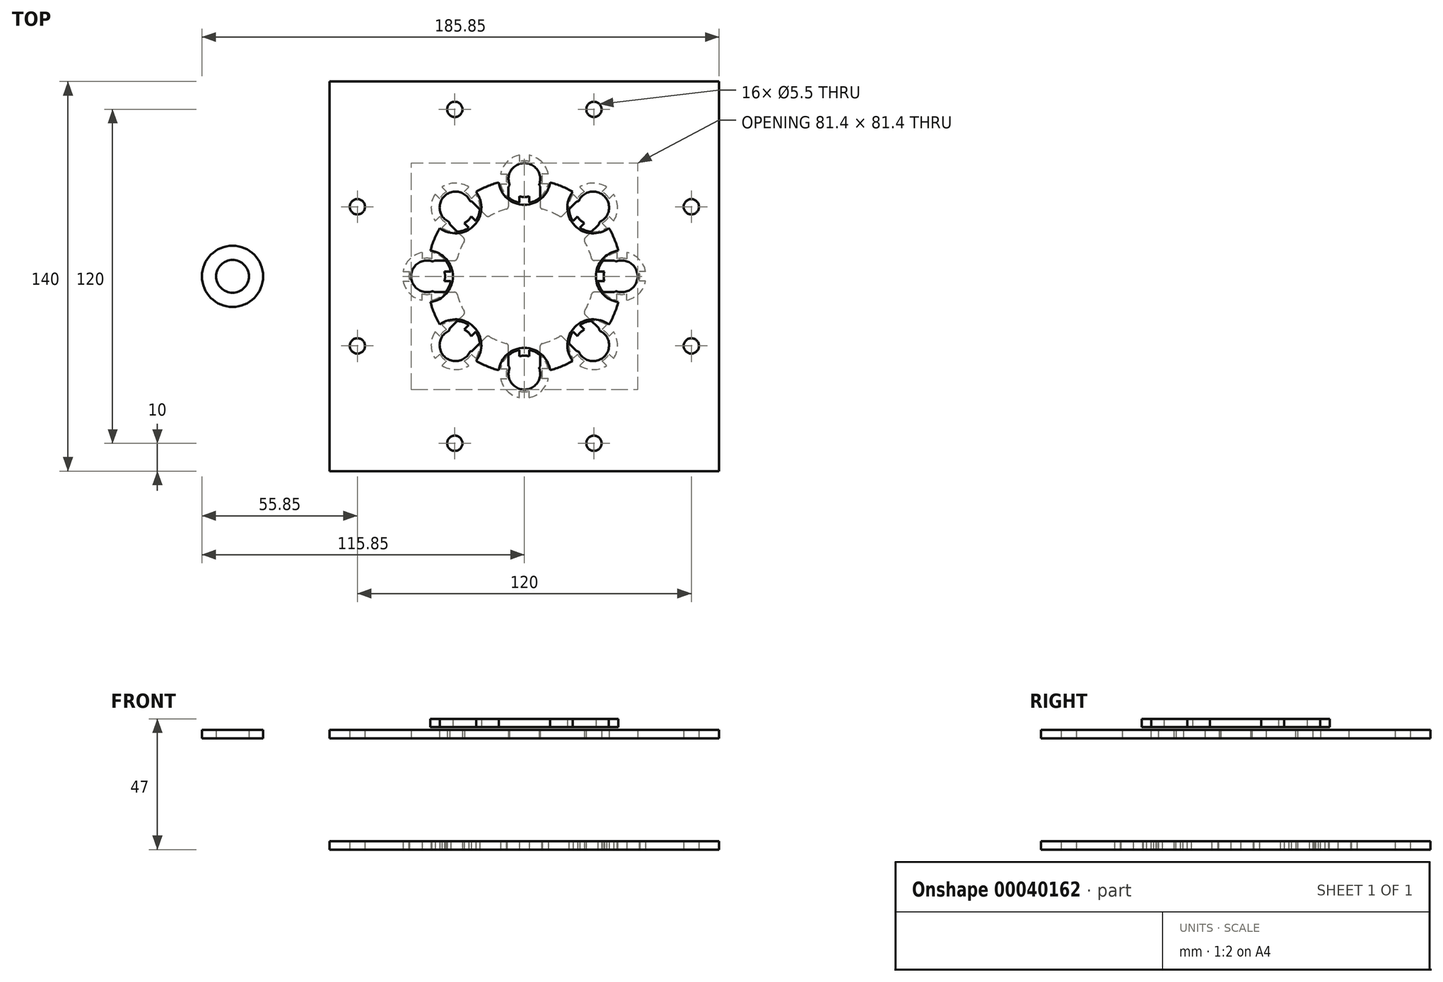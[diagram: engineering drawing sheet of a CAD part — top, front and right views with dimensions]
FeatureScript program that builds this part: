
annotation { "Feature Type Name" : "Feature", "Feature Type Description" : "" }
export const myFeature = defineFeature(function(context is Context, id is Id, definition is map)
    precondition{}
    {
        {
            var Q0;
            Q0=qCreatedBy(makeId("Top.planeOp"),FACE);
            var sketch = newSketch(context, id + "F0", { "sketchPlane" : qUnion([Q0])});
            skCircle(sketch, "E0", {"center": v(0, 0) * mm, "radius": 35 * mm, "construction": true});
            skCircle(sketch, "E1", {"center": v(0, 35) * mm, "radius": 5.7 * mm, "construction": true});
            skLineSegment(sketch, "E2.rect.bottom", {"start": v(70, 70) * mm, "end": v(-70, 70) * mm});
            skLineSegment(sketch, "E2.rect.top", {"start": v(70, -70) * mm, "end": v(-70, -70) * mm});
            skLineSegment(sketch, "E2.rect.left", {"start": v(70, 70) * mm, "end": v(70, -70) * mm});
            skLineSegment(sketch, "E2.rect.right", {"start": v(-70, 70) * mm, "end": v(-70, -70) * mm});
            skLineSegment(sketch, "E3", {"start": v(-50, 70) * mm, "end": v(-50, -70) * mm, "construction": true});
            skLineSegment(sketch, "E4", {"start": v(-70, 50) * mm, "end": v(70, 50) * mm, "construction": true});
            skLineSegment(sketch, "E5", {"start": v(-5.7, 35) * mm, "end": v(-5.7, 24.34) * mm, "construction": true});
            skLineSegment(sketch, "E6", {"start": v(5.7, 35) * mm, "end": v(5.7, 24.34) * mm, "construction": true});
            skPoint(sketch, "E7", {"position": v(-5.7, 24.34) * mm});
            skCircle(sketch, "E8", {"center": v(0, 0) * mm, "radius": 25 * mm, "construction": true});
            skLineSegment(sketch, "E9", {"start": v(-5.7, 32.2) * mm, "end": v(-5.3, 32.9) * mm});
            skLineSegment(sketch, "E10.MirrorCS", {"start": v(5.7, 32.2) * mm, "end": v(5.3, 32.9) * mm});
            skArc(sketch, "E11", {"start": v(5.3, 32.9) * mm, "mid": v(0, 40.7) * mm, "end": v(-5.3, 32.9) * mm});
            skLineSegment(sketch, "E12", {"start": v(-5.7, 32.2) * mm, "end": v(-5.7, 24.34) * mm});
            skLineSegment(sketch, "E13", {"start": v(5.7, 32.2) * mm, "end": v(5.7, 24.34) * mm});
            skLineSegment(sketch, "E14.1.0", {"start": v(-18.75, 26.8) * mm, "end": v(-13.18, 21.24) * mm});
            skLineSegment(sketch, "E14.1.1", {"start": v(-26.8, 18.75) * mm, "end": v(-21.24, 13.18) * mm});
            skLineSegment(sketch, "E14.1.2", {"start": v(-26.8, 18.75) * mm, "end": v(-27.01, 19.52) * mm});
            skLineSegment(sketch, "E14.1.3", {"start": v(-18.75, 26.8) * mm, "end": v(-19.52, 27.01) * mm});
            skArc(sketch, "E14.1.4", {"start": v(-19.52, 27.01) * mm, "mid": v(-28.78, 28.78) * mm, "end": v(-27.01, 19.52) * mm});
            skLineSegment(sketch, "E14.2.0", {"start": v(-32.2, 5.7) * mm, "end": v(-24.34, 5.7) * mm});
            skLineSegment(sketch, "E14.2.1", {"start": v(-32.2, -5.7) * mm, "end": v(-24.34, -5.7) * mm});
            skLineSegment(sketch, "E14.2.2", {"start": v(-32.2, -5.7) * mm, "end": v(-32.9, -5.3) * mm});
            skLineSegment(sketch, "E14.2.3", {"start": v(-32.2, 5.7) * mm, "end": v(-32.9, 5.3) * mm});
            skArc(sketch, "E14.2.4", {"start": v(-32.9, 5.3) * mm, "mid": v(-40.7, 0) * mm, "end": v(-32.9, -5.3) * mm});
            skLineSegment(sketch, "E14.3.0", {"start": v(-26.8, -18.75) * mm, "end": v(-21.24, -13.18) * mm});
            skLineSegment(sketch, "E14.3.1", {"start": v(-18.75, -26.8) * mm, "end": v(-13.18, -21.24) * mm});
            skLineSegment(sketch, "E14.3.2", {"start": v(-18.75, -26.8) * mm, "end": v(-19.52, -27.01) * mm});
            skLineSegment(sketch, "E14.3.3", {"start": v(-26.8, -18.75) * mm, "end": v(-27.01, -19.52) * mm});
            skArc(sketch, "E14.3.4", {"start": v(-27.01, -19.52) * mm, "mid": v(-28.78, -28.78) * mm, "end": v(-19.52, -27.01) * mm});
            skLineSegment(sketch, "E14.4.0", {"start": v(-5.7, -32.2) * mm, "end": v(-5.7, -24.34) * mm});
            skLineSegment(sketch, "E14.4.1", {"start": v(5.7, -32.2) * mm, "end": v(5.7, -24.34) * mm});
            skLineSegment(sketch, "E14.4.2", {"start": v(5.7, -32.2) * mm, "end": v(5.3, -32.9) * mm});
            skLineSegment(sketch, "E14.4.3", {"start": v(-5.7, -32.2) * mm, "end": v(-5.3, -32.9) * mm});
            skArc(sketch, "E14.4.4", {"start": v(-5.3, -32.9) * mm, "mid": v(0, -40.7) * mm, "end": v(5.3, -32.9) * mm});
            skLineSegment(sketch, "E14.5.0", {"start": v(18.75, -26.8) * mm, "end": v(13.18, -21.24) * mm});
            skLineSegment(sketch, "E14.5.1", {"start": v(26.8, -18.75) * mm, "end": v(21.24, -13.18) * mm});
            skLineSegment(sketch, "E14.5.2", {"start": v(26.8, -18.75) * mm, "end": v(27.01, -19.52) * mm});
            skLineSegment(sketch, "E14.5.3", {"start": v(18.75, -26.8) * mm, "end": v(19.52, -27.01) * mm});
            skArc(sketch, "E14.5.4", {"start": v(19.52, -27.01) * mm, "mid": v(28.78, -28.78) * mm, "end": v(27.01, -19.52) * mm});
            skLineSegment(sketch, "E14.6.0", {"start": v(32.2, -5.7) * mm, "end": v(24.34, -5.7) * mm});
            skLineSegment(sketch, "E14.6.1", {"start": v(32.2, 5.7) * mm, "end": v(24.34, 5.7) * mm});
            skLineSegment(sketch, "E14.6.2", {"start": v(32.2, 5.7) * mm, "end": v(32.9, 5.3) * mm});
            skLineSegment(sketch, "E14.6.3", {"start": v(32.2, -5.7) * mm, "end": v(32.9, -5.3) * mm});
            skArc(sketch, "E14.6.4", {"start": v(32.9, -5.3) * mm, "mid": v(40.7, 0) * mm, "end": v(32.9, 5.3) * mm});
            skLineSegment(sketch, "E14.7.0", {"start": v(26.8, 18.75) * mm, "end": v(21.24, 13.18) * mm});
            skLineSegment(sketch, "E14.7.1", {"start": v(18.75, 26.8) * mm, "end": v(13.18, 21.24) * mm});
            skLineSegment(sketch, "E14.7.2", {"start": v(18.75, 26.8) * mm, "end": v(19.52, 27.01) * mm});
            skLineSegment(sketch, "E14.7.3", {"start": v(26.8, 18.75) * mm, "end": v(27.01, 19.52) * mm});
            skArc(sketch, "E14.7.4", {"start": v(27.01, 19.52) * mm, "mid": v(28.78, 28.78) * mm, "end": v(19.52, 27.01) * mm});
            skArc(sketch, "E15", {"start": v(-5.7, 24.34) * mm, "mid": v(-9.57, 23.1) * mm, "end": v(-13.18, 21.24) * mm});
            skArc(sketch, "E16", {"start": v(13.18, 21.24) * mm, "mid": v(9.57, 23.1) * mm, "end": v(5.7, 24.34) * mm});
            skArc(sketch, "E17", {"start": v(24.34, 5.7) * mm, "mid": v(23.1, 9.57) * mm, "end": v(21.24, 13.18) * mm});
            skArc(sketch, "E18", {"start": v(-21.24, 13.18) * mm, "mid": v(-23.1, 9.57) * mm, "end": v(-24.34, 5.7) * mm});
            skArc(sketch, "E19", {"start": v(-24.34, -5.7) * mm, "mid": v(-23.1, -9.57) * mm, "end": v(-21.24, -13.18) * mm});
            skArc(sketch, "E20", {"start": v(-13.18, -21.24) * mm, "mid": v(-9.57, -23.1) * mm, "end": v(-5.7, -24.34) * mm});
            skArc(sketch, "E21", {"start": v(5.7, -24.34) * mm, "mid": v(9.57, -23.1) * mm, "end": v(13.18, -21.24) * mm});
            skArc(sketch, "E22", {"start": v(21.24, -13.18) * mm, "mid": v(23.1, -9.57) * mm, "end": v(24.34, -5.7) * mm});
            skLineSegment(sketch, "E23.rect.bottom", {"start": v(60, 60) * mm, "end": v(-60, 60) * mm, "construction": true});
            skLineSegment(sketch, "E23.rect.top", {"start": v(60, -60) * mm, "end": v(-60, -60) * mm, "construction": true});
            skLineSegment(sketch, "E23.rect.left", {"start": v(60, 60) * mm, "end": v(60, -60) * mm, "construction": true});
            skLineSegment(sketch, "E23.rect.right", {"start": v(-60, 60) * mm, "end": v(-60, -60) * mm, "construction": true});
            skCircle(sketch, "E24", {"center": v(-25, 60) * mm, "radius": 2.75 * mm});
            skCircle(sketch, "E25.MirrorC", {"center": v(25, 60) * mm, "radius": 2.75 * mm});
            skCircle(sketch, "E26.MirrorC", {"center": v(25, -60) * mm, "radius": 2.75 * mm});
            skCircle(sketch, "E27.MirrorC", {"center": v(-25, -60) * mm, "radius": 2.75 * mm});
            skCircle(sketch, "E28", {"center": v(-60, 25) * mm, "radius": 2.75 * mm});
            skCircle(sketch, "E29.MirrorC", {"center": v(-60, -25) * mm, "radius": 2.75 * mm});
            skCircle(sketch, "E30.MirrorC", {"center": v(60, 25) * mm, "radius": 2.75 * mm});
            skCircle(sketch, "E31.MirrorC", {"center": v(60, -25) * mm, "radius": 2.75 * mm});
            skSolve(sketch);
        }
        {
            var Q0;
            Q0=makeQuery(id+"F0.imprint","IMPRINT",FACE,{"disambiguationData":[TD([[makeQuery(id+"F0.imprint","IMPRINT",EDGE,{"derivedFrom":sQuery(id+"F0.wireOp",EDGE,"E2.rect.bottom")}),1.0]])]});
            extrude(context, id + "F1", {"entities" : qUnion([Q0]), "depth" : 3 * mm});
        }
        {
            var Q0;
            Q0=makeQuery(id+"F1.opExtrude","SWEPT_EDGE",EDGE,{"disambiguationData":[OSD([sQuery(id+"F0.wireOp",EDGE,"E14.1.1"),sQuery(id+"F0.wireOp",EDGE,"E18")])]});
            var Q1;
            Q1=makeQuery(id+"F1.opExtrude","SWEPT_EDGE",EDGE,{"disambiguationData":[OSD([sQuery(id+"F0.wireOp",EDGE,"E14.2.1"),sQuery(id+"F0.wireOp",EDGE,"E19")])]});
            var Q2;
            Q2=makeQuery(id+"F1.opExtrude","SWEPT_EDGE",EDGE,{"disambiguationData":[OSD([sQuery(id+"F0.wireOp",EDGE,"E14.3.0"),sQuery(id+"F0.wireOp",EDGE,"E19")])]});
            var Q3;
            Q3=makeQuery(id+"F1.opExtrude","SWEPT_EDGE",EDGE,{"disambiguationData":[OSD([sQuery(id+"F0.wireOp",EDGE,"E14.2.0"),sQuery(id+"F0.wireOp",EDGE,"E18")])]});
            var Q4;
            Q4=makeQuery(id+"F1.opExtrude","SWEPT_EDGE",EDGE,{"disambiguationData":[OSD([sQuery(id+"F0.wireOp",EDGE,"E14.1.0"),sQuery(id+"F0.wireOp",EDGE,"E15")])]});
            var Q5;
            Q5=makeQuery(id+"F1.opExtrude","SWEPT_EDGE",EDGE,{"disambiguationData":[OSD([sQuery(id+"F0.wireOp",EDGE,"E12"),sQuery(id+"F0.wireOp",EDGE,"E15")])]});
            var Q6;
            Q6=makeQuery(id+"F1.opExtrude","SWEPT_EDGE",EDGE,{"disambiguationData":[OSD([sQuery(id+"F0.wireOp",EDGE,"E14.4.0"),sQuery(id+"F0.wireOp",EDGE,"E20")])]});
            var Q7;
            Q7=makeQuery(id+"F1.opExtrude","SWEPT_EDGE",EDGE,{"disambiguationData":[OSD([sQuery(id+"F0.wireOp",EDGE,"E14.3.1"),sQuery(id+"F0.wireOp",EDGE,"E20")])]});
            var Q8;
            Q8=makeQuery(id+"F1.opExtrude","SWEPT_EDGE",EDGE,{"disambiguationData":[OSD([sQuery(id+"F0.wireOp",EDGE,"E14.5.0"),sQuery(id+"F0.wireOp",EDGE,"E21")])]});
            var Q9;
            Q9=makeQuery(id+"F1.opExtrude","SWEPT_EDGE",EDGE,{"disambiguationData":[OSD([sQuery(id+"F0.wireOp",EDGE,"E14.4.1"),sQuery(id+"F0.wireOp",EDGE,"E21")])]});
            var Q10;
            Q10=makeQuery(id+"F1.opExtrude","SWEPT_EDGE",EDGE,{"disambiguationData":[OSD([sQuery(id+"F0.wireOp",EDGE,"E14.5.1"),sQuery(id+"F0.wireOp",EDGE,"E22")])]});
            var Q11;
            Q11=makeQuery(id+"F1.opExtrude","SWEPT_EDGE",EDGE,{"disambiguationData":[OSD([sQuery(id+"F0.wireOp",EDGE,"E14.6.0"),sQuery(id+"F0.wireOp",EDGE,"E22")])]});
            var Q12;
            Q12=makeQuery(id+"F1.opExtrude","SWEPT_EDGE",EDGE,{"disambiguationData":[OSD([sQuery(id+"F0.wireOp",EDGE,"E14.6.1"),sQuery(id+"F0.wireOp",EDGE,"E17")])]});
            var Q13;
            Q13=makeQuery(id+"F1.opExtrude","SWEPT_EDGE",EDGE,{"disambiguationData":[OSD([sQuery(id+"F0.wireOp",EDGE,"E14.7.0"),sQuery(id+"F0.wireOp",EDGE,"E17")])]});
            var Q14;
            Q14=makeQuery(id+"F1.opExtrude","SWEPT_EDGE",EDGE,{"disambiguationData":[OSD([sQuery(id+"F0.wireOp",EDGE,"E14.7.1"),sQuery(id+"F0.wireOp",EDGE,"E16")])]});
            var Q15;
            Q15=makeQuery(id+"F1.opExtrude","SWEPT_EDGE",EDGE,{"disambiguationData":[OSD([sQuery(id+"F0.wireOp",EDGE,"E13"),sQuery(id+"F0.wireOp",EDGE,"E16")])]});
            fillet(context, id + "F2", {"entities" : qUnion([Q0, Q1, Q2, Q3, Q4, Q5, Q6, Q7, Q8, Q9, Q10, Q11, Q12, Q13, Q14, Q15]), "radius" : 1 * mm, "tangentPropagation" : true, "allowEdgeOverflow" : false});
        }
        {
            var Q0;
            Q0=qCreatedBy(makeId("Top.planeOp"),FACE);
            cPlane(context, id + "F3", {"entities" : qUnion([Q0]), "cplaneType" : CPlaneType.OFFSET, "offset" : 40 * mm, "oppositeDirection" : true, "width" : 150 * mm, "height" : 150 * mm});
        }
        {
            var Q0;
            Q0=qCreatedBy(id+"F3.planeOp",FACE);
            var sketch = newSketch(context, id + "F4", { "sketchPlane" : qUnion([Q0])});
            skArc(sketch, "E32", {"start": v(8.57, -33.25) * mm, "mid": v(6.19, -28.81) * mm, "end": v(1.75, -26.43) * mm});
            skLineSegment(sketch, "E33.rect.right", {"start": v(1.75, -26.43) * mm, "end": v(1.75, -28.74) * mm});
            skArc(sketch, "E34", {"start": v(1.75, -28.74) * mm, "mid": v(0, -28.5) * mm, "end": v(-1.75, -28.74) * mm});
            skLineSegment(sketch, "E33.rect.left", {"start": v(-1.75, -26.43) * mm, "end": v(-1.75, -28.74) * mm});
            skArc(sketch, "E35", {"start": v(-1.75, -26.43) * mm, "mid": v(-6.19, -28.81) * mm, "end": v(-8.57, -33.25) * mm});
            skLineSegment(sketch, "E36.1.1", {"start": v(-8.57, -33.25) * mm, "end": v(-6.26, -33.25) * mm});
            skArc(sketch, "E36.1.2", {"start": v(-6.26, -33.25) * mm, "mid": v(-6.5, -35) * mm, "end": v(-6.26, -36.75) * mm});
            skArc(sketch, "E37", {"start": v(-1.75, -28.74) * mm, "mid": v(0, -41.5) * mm, "end": v(1.75, -28.74) * mm, "construction": true});
            skLineSegment(sketch, "E36.1.0", {"start": v(-8.57, -36.75) * mm, "end": v(-6.26, -36.75) * mm});
            skArc(sketch, "E38", {"start": v(-8.57, -33.25) * mm, "mid": v(-8.75, -35) * mm, "end": v(-8.57, -36.75) * mm, "construction": true});
            skArc(sketch, "E39", {"start": v(-8.57, -36.75) * mm, "mid": v(-6.19, -41.19) * mm, "end": v(-1.75, -43.57) * mm});
            skLineSegment(sketch, "E36.2.1", {"start": v(-1.75, -43.57) * mm, "end": v(-1.75, -41.26) * mm});
            skArc(sketch, "E36.2.2", {"start": v(-1.75, -41.26) * mm, "mid": v(0, -41.5) * mm, "end": v(1.75, -41.26) * mm});
            skLineSegment(sketch, "E36.2.0", {"start": v(1.75, -43.57) * mm, "end": v(1.75, -41.26) * mm});
            skArc(sketch, "E40", {"start": v(-1.75, -43.57) * mm, "mid": v(0, -43.75) * mm, "end": v(1.75, -43.57) * mm, "construction": true});
            skArc(sketch, "E41", {"start": v(1.75, -43.57) * mm, "mid": v(6.19, -41.19) * mm, "end": v(8.57, -36.75) * mm});
            skLineSegment(sketch, "E36.3.1", {"start": v(8.57, -36.75) * mm, "end": v(6.26, -36.75) * mm});
            skArc(sketch, "E42", {"start": v(8.57, -36.75) * mm, "mid": v(8.75, -35) * mm, "end": v(8.57, -33.25) * mm, "construction": true});
            skLineSegment(sketch, "E36.3.0", {"start": v(8.57, -33.25) * mm, "end": v(6.26, -33.25) * mm});
            skArc(sketch, "E36.3.2", {"start": v(6.26, -36.75) * mm, "mid": v(6.5, -35) * mm, "end": v(6.26, -33.25) * mm});
            skLineSegment(sketch, "E33.rect.bottom", {"start": v(-1.75, -26.43) * mm, "end": v(1.75, -26.43) * mm, "construction": true});
            skArc(sketch, "E43", {"start": v(1.75, -26.43) * mm, "mid": v(0, -26.25) * mm, "end": v(-1.75, -26.43) * mm, "construction": true});
            skLineSegment(sketch, "E33.rect.top", {"start": v(-1.75, -28.74) * mm, "end": v(1.75, -28.74) * mm, "construction": true});
            skLineSegment(sketch, "E44.rect.bottom", {"start": v(70, -70) * mm, "end": v(-70, -70) * mm});
            skLineSegment(sketch, "E44.rect.top", {"start": v(70, 70) * mm, "end": v(-70, 70) * mm});
            skLineSegment(sketch, "E44.rect.left", {"start": v(70, -70) * mm, "end": v(70, 70) * mm});
            skLineSegment(sketch, "E44.rect.right", {"start": v(-70, -70) * mm, "end": v(-70, 70) * mm});
            skPoint(sketch, "E44.rect.middle", {"position": v(0, 0) * mm});
            skLineSegment(sketch, "E45.1.1", {"start": v(29.57, -17.45) * mm, "end": v(27.94, -19.08) * mm});
            skArc(sketch, "E45.1.2", {"start": v(30.41, -21.56) * mm, "mid": v(29.34, -20.15) * mm, "end": v(27.94, -19.08) * mm});
            skLineSegment(sketch, "E45.1.3", {"start": v(32.05, -19.92) * mm, "end": v(30.41, -21.56) * mm});
            skArc(sketch, "E45.1.4", {"start": v(32.05, -29.57) * mm, "mid": v(33.5, -24.75) * mm, "end": v(32.05, -19.92) * mm});
            skArc(sketch, "E45.1.5", {"start": v(29.57, -17.45) * mm, "mid": v(24.75, -16) * mm, "end": v(19.92, -17.45) * mm});
            skLineSegment(sketch, "E45.1.6", {"start": v(19.92, -17.45) * mm, "end": v(21.56, -19.08) * mm});
            skArc(sketch, "E45.1.7", {"start": v(21.56, -19.08) * mm, "mid": v(20.15, -20.15) * mm, "end": v(19.08, -21.56) * mm});
            skLineSegment(sketch, "E45.1.8", {"start": v(17.45, -19.92) * mm, "end": v(19.08, -21.56) * mm});
            skArc(sketch, "E45.1.9", {"start": v(17.45, -19.92) * mm, "mid": v(16, -24.75) * mm, "end": v(17.45, -29.57) * mm});
            skLineSegment(sketch, "E45.1.10", {"start": v(17.45, -29.57) * mm, "end": v(19.08, -27.94) * mm});
            skArc(sketch, "E45.1.11", {"start": v(19.08, -27.94) * mm, "mid": v(20.15, -29.34) * mm, "end": v(21.56, -30.41) * mm});
            skLineSegment(sketch, "E45.1.12", {"start": v(19.92, -32.05) * mm, "end": v(21.56, -30.41) * mm});
            skArc(sketch, "E45.1.13", {"start": v(19.92, -32.05) * mm, "mid": v(24.75, -33.5) * mm, "end": v(29.57, -32.05) * mm});
            skArc(sketch, "E45.1.14", {"start": v(27.94, -30.41) * mm, "mid": v(29.34, -29.34) * mm, "end": v(30.41, -27.94) * mm});
            skLineSegment(sketch, "E45.1.15", {"start": v(29.57, -32.05) * mm, "end": v(27.94, -30.41) * mm});
            skLineSegment(sketch, "E45.1.16", {"start": v(32.05, -29.57) * mm, "end": v(30.41, -27.94) * mm});
            skLineSegment(sketch, "E45.2.1", {"start": v(33.25, 8.57) * mm, "end": v(33.25, 6.26) * mm});
            skArc(sketch, "E45.2.2", {"start": v(36.75, 6.26) * mm, "mid": v(35, 6.5) * mm, "end": v(33.25, 6.26) * mm});
            skLineSegment(sketch, "E45.2.3", {"start": v(36.75, 8.57) * mm, "end": v(36.75, 6.26) * mm});
            skArc(sketch, "E45.2.4", {"start": v(43.57, 1.75) * mm, "mid": v(41.19, 6.19) * mm, "end": v(36.75, 8.57) * mm});
            skArc(sketch, "E45.2.5", {"start": v(33.25, 8.57) * mm, "mid": v(28.81, 6.19) * mm, "end": v(26.43, 1.75) * mm});
            skLineSegment(sketch, "E45.2.6", {"start": v(26.43, 1.75) * mm, "end": v(28.74, 1.75) * mm});
            skArc(sketch, "E45.2.7", {"start": v(28.74, 1.75) * mm, "mid": v(28.5, 0) * mm, "end": v(28.74, -1.75) * mm});
            skLineSegment(sketch, "E45.2.8", {"start": v(26.43, -1.75) * mm, "end": v(28.74, -1.75) * mm});
            skArc(sketch, "E45.2.9", {"start": v(26.43, -1.75) * mm, "mid": v(28.81, -6.19) * mm, "end": v(33.25, -8.57) * mm});
            skLineSegment(sketch, "E45.2.10", {"start": v(33.25, -8.57) * mm, "end": v(33.25, -6.26) * mm});
            skArc(sketch, "E45.2.11", {"start": v(33.25, -6.26) * mm, "mid": v(35, -6.5) * mm, "end": v(36.75, -6.26) * mm});
            skLineSegment(sketch, "E45.2.12", {"start": v(36.75, -8.57) * mm, "end": v(36.75, -6.26) * mm});
            skArc(sketch, "E45.2.13", {"start": v(36.75, -8.57) * mm, "mid": v(41.19, -6.19) * mm, "end": v(43.57, -1.75) * mm});
            skArc(sketch, "E45.2.14", {"start": v(41.26, -1.75) * mm, "mid": v(41.5, 0) * mm, "end": v(41.26, 1.75) * mm});
            skLineSegment(sketch, "E45.2.15", {"start": v(43.57, -1.75) * mm, "end": v(41.26, -1.75) * mm});
            skLineSegment(sketch, "E45.2.16", {"start": v(43.57, 1.75) * mm, "end": v(41.26, 1.75) * mm});
            skLineSegment(sketch, "E45.3.1", {"start": v(17.45, 29.57) * mm, "end": v(19.08, 27.94) * mm});
            skArc(sketch, "E45.3.2", {"start": v(21.56, 30.41) * mm, "mid": v(20.15, 29.34) * mm, "end": v(19.08, 27.94) * mm});
            skLineSegment(sketch, "E45.3.3", {"start": v(19.92, 32.05) * mm, "end": v(21.56, 30.41) * mm});
            skArc(sketch, "E45.3.4", {"start": v(29.57, 32.05) * mm, "mid": v(24.75, 33.5) * mm, "end": v(19.92, 32.05) * mm});
            skArc(sketch, "E45.3.5", {"start": v(17.45, 29.57) * mm, "mid": v(16, 24.75) * mm, "end": v(17.45, 19.92) * mm});
            skLineSegment(sketch, "E45.3.6", {"start": v(17.45, 19.92) * mm, "end": v(19.08, 21.56) * mm});
            skArc(sketch, "E45.3.7", {"start": v(19.08, 21.56) * mm, "mid": v(20.15, 20.15) * mm, "end": v(21.56, 19.08) * mm});
            skLineSegment(sketch, "E45.3.8", {"start": v(19.92, 17.45) * mm, "end": v(21.56, 19.08) * mm});
            skArc(sketch, "E45.3.9", {"start": v(19.92, 17.45) * mm, "mid": v(24.75, 16) * mm, "end": v(29.57, 17.45) * mm});
            skLineSegment(sketch, "E45.3.10", {"start": v(29.57, 17.45) * mm, "end": v(27.94, 19.08) * mm});
            skArc(sketch, "E45.3.11", {"start": v(27.94, 19.08) * mm, "mid": v(29.34, 20.15) * mm, "end": v(30.41, 21.56) * mm});
            skLineSegment(sketch, "E45.3.12", {"start": v(32.05, 19.92) * mm, "end": v(30.41, 21.56) * mm});
            skArc(sketch, "E45.3.13", {"start": v(32.05, 19.92) * mm, "mid": v(33.5, 24.75) * mm, "end": v(32.05, 29.57) * mm});
            skArc(sketch, "E45.3.14", {"start": v(30.41, 27.94) * mm, "mid": v(29.34, 29.34) * mm, "end": v(27.94, 30.41) * mm});
            skLineSegment(sketch, "E45.3.15", {"start": v(32.05, 29.57) * mm, "end": v(30.41, 27.94) * mm});
            skLineSegment(sketch, "E45.3.16", {"start": v(29.57, 32.05) * mm, "end": v(27.94, 30.41) * mm});
            skLineSegment(sketch, "E45.4.1", {"start": v(-8.57, 33.25) * mm, "end": v(-6.26, 33.25) * mm});
            skArc(sketch, "E45.4.2", {"start": v(-6.26, 36.75) * mm, "mid": v(-6.5, 35) * mm, "end": v(-6.26, 33.25) * mm});
            skLineSegment(sketch, "E45.4.3", {"start": v(-8.57, 36.75) * mm, "end": v(-6.26, 36.75) * mm});
            skArc(sketch, "E45.4.4", {"start": v(-1.75, 43.57) * mm, "mid": v(-6.19, 41.19) * mm, "end": v(-8.57, 36.75) * mm});
            skArc(sketch, "E45.4.5", {"start": v(-8.57, 33.25) * mm, "mid": v(-6.19, 28.81) * mm, "end": v(-1.75, 26.43) * mm});
            skLineSegment(sketch, "E45.4.6", {"start": v(-1.75, 26.43) * mm, "end": v(-1.75, 28.74) * mm});
            skArc(sketch, "E45.4.7", {"start": v(-1.75, 28.74) * mm, "mid": v(0, 28.5) * mm, "end": v(1.75, 28.74) * mm});
            skLineSegment(sketch, "E45.4.8", {"start": v(1.75, 26.43) * mm, "end": v(1.75, 28.74) * mm});
            skArc(sketch, "E45.4.9", {"start": v(1.75, 26.43) * mm, "mid": v(6.19, 28.81) * mm, "end": v(8.57, 33.25) * mm});
            skLineSegment(sketch, "E45.4.10", {"start": v(8.57, 33.25) * mm, "end": v(6.26, 33.25) * mm});
            skArc(sketch, "E45.4.11", {"start": v(6.26, 33.25) * mm, "mid": v(6.5, 35) * mm, "end": v(6.26, 36.75) * mm});
            skLineSegment(sketch, "E45.4.12", {"start": v(8.57, 36.75) * mm, "end": v(6.26, 36.75) * mm});
            skArc(sketch, "E45.4.13", {"start": v(8.57, 36.75) * mm, "mid": v(6.19, 41.19) * mm, "end": v(1.75, 43.57) * mm});
            skArc(sketch, "E45.4.14", {"start": v(1.75, 41.26) * mm, "mid": v(0, 41.5) * mm, "end": v(-1.75, 41.26) * mm});
            skLineSegment(sketch, "E45.4.15", {"start": v(1.75, 43.57) * mm, "end": v(1.75, 41.26) * mm});
            skLineSegment(sketch, "E45.4.16", {"start": v(-1.75, 43.57) * mm, "end": v(-1.75, 41.26) * mm});
            skLineSegment(sketch, "E45.5.1", {"start": v(-29.57, 17.45) * mm, "end": v(-27.94, 19.08) * mm});
            skArc(sketch, "E45.5.2", {"start": v(-30.41, 21.56) * mm, "mid": v(-29.34, 20.15) * mm, "end": v(-27.94, 19.08) * mm});
            skLineSegment(sketch, "E45.5.3", {"start": v(-32.05, 19.92) * mm, "end": v(-30.41, 21.56) * mm});
            skArc(sketch, "E45.5.4", {"start": v(-32.05, 29.57) * mm, "mid": v(-33.5, 24.75) * mm, "end": v(-32.05, 19.92) * mm});
            skArc(sketch, "E45.5.5", {"start": v(-29.57, 17.45) * mm, "mid": v(-24.75, 16) * mm, "end": v(-19.92, 17.45) * mm});
            skLineSegment(sketch, "E45.5.6", {"start": v(-19.92, 17.45) * mm, "end": v(-21.56, 19.08) * mm});
            skArc(sketch, "E45.5.7", {"start": v(-21.56, 19.08) * mm, "mid": v(-20.15, 20.15) * mm, "end": v(-19.08, 21.56) * mm});
            skLineSegment(sketch, "E45.5.8", {"start": v(-17.45, 19.92) * mm, "end": v(-19.08, 21.56) * mm});
            skArc(sketch, "E45.5.9", {"start": v(-17.45, 19.92) * mm, "mid": v(-16, 24.75) * mm, "end": v(-17.45, 29.57) * mm});
            skLineSegment(sketch, "E45.5.10", {"start": v(-17.45, 29.57) * mm, "end": v(-19.08, 27.94) * mm});
            skArc(sketch, "E45.5.11", {"start": v(-19.08, 27.94) * mm, "mid": v(-20.15, 29.34) * mm, "end": v(-21.56, 30.41) * mm});
            skLineSegment(sketch, "E45.5.12", {"start": v(-19.92, 32.05) * mm, "end": v(-21.56, 30.41) * mm});
            skArc(sketch, "E45.5.13", {"start": v(-19.92, 32.05) * mm, "mid": v(-24.75, 33.5) * mm, "end": v(-29.57, 32.05) * mm});
            skArc(sketch, "E45.5.14", {"start": v(-27.94, 30.41) * mm, "mid": v(-29.34, 29.34) * mm, "end": v(-30.41, 27.94) * mm});
            skLineSegment(sketch, "E45.5.15", {"start": v(-29.57, 32.05) * mm, "end": v(-27.94, 30.41) * mm});
            skLineSegment(sketch, "E45.5.16", {"start": v(-32.05, 29.57) * mm, "end": v(-30.41, 27.94) * mm});
            skLineSegment(sketch, "E45.6.1", {"start": v(-33.25, -8.57) * mm, "end": v(-33.25, -6.26) * mm});
            skArc(sketch, "E45.6.2", {"start": v(-36.75, -6.26) * mm, "mid": v(-35, -6.5) * mm, "end": v(-33.25, -6.26) * mm});
            skLineSegment(sketch, "E45.6.3", {"start": v(-36.75, -8.57) * mm, "end": v(-36.75, -6.26) * mm});
            skArc(sketch, "E45.6.4", {"start": v(-43.57, -1.75) * mm, "mid": v(-41.19, -6.19) * mm, "end": v(-36.75, -8.57) * mm});
            skArc(sketch, "E45.6.5", {"start": v(-33.25, -8.57) * mm, "mid": v(-28.81, -6.19) * mm, "end": v(-26.43, -1.75) * mm});
            skLineSegment(sketch, "E45.6.6", {"start": v(-26.43, -1.75) * mm, "end": v(-28.74, -1.75) * mm});
            skArc(sketch, "E45.6.7", {"start": v(-28.74, -1.75) * mm, "mid": v(-28.5, 0) * mm, "end": v(-28.74, 1.75) * mm});
            skLineSegment(sketch, "E45.6.8", {"start": v(-26.43, 1.75) * mm, "end": v(-28.74, 1.75) * mm});
            skArc(sketch, "E45.6.9", {"start": v(-26.43, 1.75) * mm, "mid": v(-28.81, 6.19) * mm, "end": v(-33.25, 8.57) * mm});
            skLineSegment(sketch, "E45.6.10", {"start": v(-33.25, 8.57) * mm, "end": v(-33.25, 6.26) * mm});
            skArc(sketch, "E45.6.11", {"start": v(-33.25, 6.26) * mm, "mid": v(-35, 6.5) * mm, "end": v(-36.75, 6.26) * mm});
            skLineSegment(sketch, "E45.6.12", {"start": v(-36.75, 8.57) * mm, "end": v(-36.75, 6.26) * mm});
            skArc(sketch, "E45.6.13", {"start": v(-36.75, 8.57) * mm, "mid": v(-41.19, 6.19) * mm, "end": v(-43.57, 1.75) * mm});
            skArc(sketch, "E45.6.14", {"start": v(-41.26, 1.75) * mm, "mid": v(-41.5, 0) * mm, "end": v(-41.26, -1.75) * mm});
            skLineSegment(sketch, "E45.6.15", {"start": v(-43.57, 1.75) * mm, "end": v(-41.26, 1.75) * mm});
            skLineSegment(sketch, "E45.6.16", {"start": v(-43.57, -1.75) * mm, "end": v(-41.26, -1.75) * mm});
            skLineSegment(sketch, "E45.7.1", {"start": v(-17.45, -29.57) * mm, "end": v(-19.08, -27.94) * mm});
            skArc(sketch, "E45.7.2", {"start": v(-21.56, -30.41) * mm, "mid": v(-20.15, -29.34) * mm, "end": v(-19.08, -27.94) * mm});
            skLineSegment(sketch, "E45.7.3", {"start": v(-19.92, -32.05) * mm, "end": v(-21.56, -30.41) * mm});
            skArc(sketch, "E45.7.4", {"start": v(-29.57, -32.05) * mm, "mid": v(-24.75, -33.5) * mm, "end": v(-19.92, -32.05) * mm});
            skArc(sketch, "E45.7.5", {"start": v(-17.45, -29.57) * mm, "mid": v(-16, -24.75) * mm, "end": v(-17.45, -19.92) * mm});
            skLineSegment(sketch, "E45.7.6", {"start": v(-17.45, -19.92) * mm, "end": v(-19.08, -21.56) * mm});
            skArc(sketch, "E45.7.7", {"start": v(-19.08, -21.56) * mm, "mid": v(-20.15, -20.15) * mm, "end": v(-21.56, -19.08) * mm});
            skLineSegment(sketch, "E45.7.8", {"start": v(-19.92, -17.45) * mm, "end": v(-21.56, -19.08) * mm});
            skArc(sketch, "E45.7.9", {"start": v(-19.92, -17.45) * mm, "mid": v(-24.75, -16) * mm, "end": v(-29.57, -17.45) * mm});
            skLineSegment(sketch, "E45.7.10", {"start": v(-29.57, -17.45) * mm, "end": v(-27.94, -19.08) * mm});
            skArc(sketch, "E45.7.11", {"start": v(-27.94, -19.08) * mm, "mid": v(-29.34, -20.15) * mm, "end": v(-30.41, -21.56) * mm});
            skLineSegment(sketch, "E45.7.12", {"start": v(-32.05, -19.92) * mm, "end": v(-30.41, -21.56) * mm});
            skArc(sketch, "E45.7.13", {"start": v(-32.05, -19.92) * mm, "mid": v(-33.5, -24.75) * mm, "end": v(-32.05, -29.57) * mm});
            skArc(sketch, "E45.7.14", {"start": v(-30.41, -27.94) * mm, "mid": v(-29.34, -29.34) * mm, "end": v(-27.94, -30.41) * mm});
            skLineSegment(sketch, "E45.7.15", {"start": v(-32.05, -29.57) * mm, "end": v(-30.41, -27.94) * mm});
            skLineSegment(sketch, "E45.7.16", {"start": v(-29.57, -32.05) * mm, "end": v(-27.94, -30.41) * mm});
            skCircle(sketch, "E46", {"center": v(-25, -60) * mm, "radius": 2.75 * mm});
            skCircle(sketch, "E47", {"center": v(25, -60) * mm, "radius": 2.75 * mm});
            skCircle(sketch, "E48", {"center": v(-60, -25) * mm, "radius": 2.75 * mm});
            skCircle(sketch, "E49", {"center": v(60, -25) * mm, "radius": 2.75 * mm});
            skCircle(sketch, "E50.MirrorC", {"center": v(-60, 25) * mm, "radius": 2.75 * mm});
            skCircle(sketch, "E51.MirrorC", {"center": v(-25, 60) * mm, "radius": 2.75 * mm});
            skCircle(sketch, "E52.MirrorC", {"center": v(25, 60) * mm, "radius": 2.75 * mm});
            skCircle(sketch, "E53.MirrorC", {"center": v(60, 25) * mm, "radius": 2.75 * mm});
            skSolve(sketch);
        }
        {
            var Q0;
            Q0=makeQuery(id+"F4.imprint","IMPRINT",FACE,{"disambiguationData":[TD([[makeQuery(id+"F4.imprint","IMPRINT",EDGE,{"derivedFrom":sQuery(id+"F4.wireOp",EDGE,"E32")}),-1.0]])]});
            extrude(context, id + "F5", {"entities" : qUnion([Q0]), "depth" : 3 * mm});
        }
        {
            var Q0;
            Q0=makeQuery(id+"F1.opExtrude","SWEPT_EDGE",EDGE,{"disambiguationData":[OSD([sQuery(id+"F0.wireOp",EDGE,"E14.3.2"),sQuery(id+"F0.wireOp",EDGE,"E14.3.4")])]});
            var Q1;
            Q1=makeQuery(id+"F1.opExtrude","SWEPT_EDGE",EDGE,{"disambiguationData":[OSD([sQuery(id+"F0.wireOp",EDGE,"E14.3.1"),sQuery(id+"F0.wireOp",EDGE,"E14.3.2")])]});
            var Q2;
            Q2=makeQuery(id+"F1.opExtrude","SWEPT_EDGE",EDGE,{"disambiguationData":[OSD([sQuery(id+"F0.wireOp",EDGE,"E14.3.3"),sQuery(id+"F0.wireOp",EDGE,"E14.3.4")])]});
            var Q3;
            Q3=makeQuery(id+"F1.opExtrude","SWEPT_EDGE",EDGE,{"disambiguationData":[OSD([sQuery(id+"F0.wireOp",EDGE,"E14.4.3"),sQuery(id+"F0.wireOp",EDGE,"E14.4.4")])]});
            var Q4;
            Q4=makeQuery(id+"F1.opExtrude","SWEPT_EDGE",EDGE,{"disambiguationData":[OSD([sQuery(id+"F0.wireOp",EDGE,"E14.4.0"),sQuery(id+"F0.wireOp",EDGE,"E14.4.3")])]});
            var Q5;
            Q5=makeQuery(id+"F1.opExtrude","SWEPT_EDGE",EDGE,{"disambiguationData":[OSD([sQuery(id+"F0.wireOp",EDGE,"E14.4.2"),sQuery(id+"F0.wireOp",EDGE,"E14.4.4")])]});
            var Q6;
            Q6=makeQuery(id+"F1.opExtrude","SWEPT_EDGE",EDGE,{"disambiguationData":[OSD([sQuery(id+"F0.wireOp",EDGE,"E14.4.1"),sQuery(id+"F0.wireOp",EDGE,"E14.4.2")])]});
            var Q7;
            Q7=makeQuery(id+"F1.opExtrude","SWEPT_EDGE",EDGE,{"disambiguationData":[OSD([sQuery(id+"F0.wireOp",EDGE,"E14.2.2"),sQuery(id+"F0.wireOp",EDGE,"E14.2.4")])]});
            var Q8;
            Q8=makeQuery(id+"F1.opExtrude","SWEPT_EDGE",EDGE,{"disambiguationData":[OSD([sQuery(id+"F0.wireOp",EDGE,"E14.2.1"),sQuery(id+"F0.wireOp",EDGE,"E14.2.2")])]});
            var Q9;
            Q9=makeQuery(id+"F1.opExtrude","SWEPT_EDGE",EDGE,{"disambiguationData":[OSD([sQuery(id+"F0.wireOp",EDGE,"E14.2.3"),sQuery(id+"F0.wireOp",EDGE,"E14.2.4")])]});
            var Q10;
            Q10=makeQuery(id+"F1.opExtrude","SWEPT_EDGE",EDGE,{"disambiguationData":[OSD([sQuery(id+"F0.wireOp",EDGE,"E14.2.0"),sQuery(id+"F0.wireOp",EDGE,"E14.2.3")])]});
            var Q11;
            Q11=makeQuery(id+"F1.opExtrude","SWEPT_EDGE",EDGE,{"disambiguationData":[OSD([sQuery(id+"F0.wireOp",EDGE,"E14.1.3"),sQuery(id+"F0.wireOp",EDGE,"E14.1.4")])]});
            var Q12;
            Q12=makeQuery(id+"F1.opExtrude","SWEPT_EDGE",EDGE,{"disambiguationData":[OSD([sQuery(id+"F0.wireOp",EDGE,"E14.1.0"),sQuery(id+"F0.wireOp",EDGE,"E14.1.3")])]});
            var Q13;
            Q13=makeQuery(id+"F1.opExtrude","SWEPT_EDGE",EDGE,{"disambiguationData":[OSD([sQuery(id+"F0.wireOp",EDGE,"E9"),sQuery(id+"F0.wireOp",EDGE,"E12")])]});
            var Q14;
            Q14=makeQuery(id+"F1.opExtrude","SWEPT_EDGE",EDGE,{"disambiguationData":[OSD([sQuery(id+"F0.wireOp",EDGE,"E9"),sQuery(id+"F0.wireOp",EDGE,"E11")])]});
            var Q15;
            Q15=makeQuery(id+"F1.opExtrude","SWEPT_EDGE",EDGE,{"disambiguationData":[OSD([sQuery(id+"F0.wireOp",EDGE,"E14.7.1"),sQuery(id+"F0.wireOp",EDGE,"E14.7.2")])]});
            var Q16;
            Q16=makeQuery(id+"F1.opExtrude","SWEPT_EDGE",EDGE,{"disambiguationData":[OSD([sQuery(id+"F0.wireOp",EDGE,"E14.7.2"),sQuery(id+"F0.wireOp",EDGE,"E14.7.4")])]});
            var Q17;
            Q17=makeQuery(id+"F1.opExtrude","SWEPT_EDGE",EDGE,{"disambiguationData":[OSD([sQuery(id+"F0.wireOp",EDGE,"E14.6.1"),sQuery(id+"F0.wireOp",EDGE,"E14.6.2")])]});
            var Q18;
            Q18=makeQuery(id+"F1.opExtrude","SWEPT_EDGE",EDGE,{"disambiguationData":[OSD([sQuery(id+"F0.wireOp",EDGE,"E14.6.2"),sQuery(id+"F0.wireOp",EDGE,"E14.6.4")])]});
            var Q19;
            Q19=makeQuery(id+"F1.opExtrude","SWEPT_EDGE",EDGE,{"disambiguationData":[OSD([sQuery(id+"F0.wireOp",EDGE,"E14.5.2"),sQuery(id+"F0.wireOp",EDGE,"E14.5.4")])]});
            var Q20;
            Q20=makeQuery(id+"F1.opExtrude","SWEPT_EDGE",EDGE,{"disambiguationData":[OSD([sQuery(id+"F0.wireOp",EDGE,"E14.5.1"),sQuery(id+"F0.wireOp",EDGE,"E14.5.2")])]});
            var Q21;
            Q21=makeQuery(id+"F1.opExtrude","SWEPT_EDGE",EDGE,{"disambiguationData":[OSD([sQuery(id+"F0.wireOp",EDGE,"E14.5.3"),sQuery(id+"F0.wireOp",EDGE,"E14.5.4")])]});
            var Q22;
            Q22=makeQuery(id+"F1.opExtrude","SWEPT_EDGE",EDGE,{"disambiguationData":[OSD([sQuery(id+"F0.wireOp",EDGE,"E14.5.0"),sQuery(id+"F0.wireOp",EDGE,"E14.5.3")])]});
            var Q23;
            Q23=makeQuery(id+"F1.opExtrude","SWEPT_EDGE",EDGE,{"disambiguationData":[OSD([sQuery(id+"F0.wireOp",EDGE,"E14.7.3"),sQuery(id+"F0.wireOp",EDGE,"E14.7.4")])]});
            var Q24;
            Q24=makeQuery(id+"F1.opExtrude","SWEPT_EDGE",EDGE,{"disambiguationData":[OSD([sQuery(id+"F0.wireOp",EDGE,"E14.7.0"),sQuery(id+"F0.wireOp",EDGE,"E14.7.3")])]});
            var Q25;
            Q25=makeQuery(id+"F1.opExtrude","SWEPT_EDGE",EDGE,{"disambiguationData":[OSD([sQuery(id+"F0.wireOp",EDGE,"E10.MirrorCS"),sQuery(id+"F0.wireOp",EDGE,"E11")])]});
            var Q26;
            Q26=makeQuery(id+"F1.opExtrude","SWEPT_EDGE",EDGE,{"disambiguationData":[OSD([sQuery(id+"F0.wireOp",EDGE,"E10.MirrorCS"),sQuery(id+"F0.wireOp",EDGE,"E13")])]});
            var Q27;
            Q27=makeQuery(id+"F1.opExtrude","SWEPT_EDGE",EDGE,{"disambiguationData":[OSD([sQuery(id+"F0.wireOp",EDGE,"E14.1.2"),sQuery(id+"F0.wireOp",EDGE,"E14.1.4")])]});
            var Q28;
            Q28=makeQuery(id+"F1.opExtrude","SWEPT_EDGE",EDGE,{"disambiguationData":[OSD([sQuery(id+"F0.wireOp",EDGE,"E14.1.1"),sQuery(id+"F0.wireOp",EDGE,"E14.1.2")])]});
            var Q29;
            Q29=makeQuery(id+"F1.opExtrude","SWEPT_EDGE",EDGE,{"disambiguationData":[OSD([sQuery(id+"F0.wireOp",EDGE,"E14.6.3"),sQuery(id+"F0.wireOp",EDGE,"E14.6.4")])]});
            var Q30;
            Q30=makeQuery(id+"F1.opExtrude","SWEPT_EDGE",EDGE,{"disambiguationData":[OSD([sQuery(id+"F0.wireOp",EDGE,"E14.6.0"),sQuery(id+"F0.wireOp",EDGE,"E14.6.3")])]});
            fillet(context, id + "F6", {"entities" : qUnion([Q0, Q1, Q2, Q3, Q4, Q5, Q6, Q7, Q8, Q9, Q10, Q11, Q12, Q13, Q14, Q15, Q16, Q17, Q18, Q19, Q20, Q21, Q22, Q23, Q24, Q25, Q26, Q27, Q28, Q29, Q30]), "radius" : 0.5 * mm, "tangentPropagation" : true, "allowEdgeOverflow" : false});
        }
        {
            var Q0;
            Q0=qCreatedBy(makeId("Top.planeOp"),FACE);
            cPlane(context, id + "F7", {"entities" : qUnion([Q0]), "cplaneType" : CPlaneType.OFFSET, "offset" : 4 * mm, "width" : 150 * mm, "height" : 150 * mm});
        }
        {
            var Q0;
            Q0=qCreatedBy(id+"F7.planeOp",FACE);
            var sketch = newSketch(context, id + "F8", { "sketchPlane" : qUnion([Q0])});
            skCircle(sketch, "E54", {"center": v(0, 35) * mm, "radius": 9.3 * mm, "construction": true});
            skCircle(sketch, "E55", {"center": v(0, 0) * mm, "radius": 35 * mm});
            skArc(sketch, "E56", {"start": v(-9.22, 33.76) * mm, "mid": v(0, 25.7) * mm, "end": v(9.22, 33.76) * mm});
            skArc(sketch, "E57.1.0", {"start": v(-30.4, 17.36) * mm, "mid": v(-18.17, 18.17) * mm, "end": v(-17.36, 30.4) * mm});
            skArc(sketch, "E57.2.0", {"start": v(-33.76, -9.22) * mm, "mid": v(-25.7, 0) * mm, "end": v(-33.76, 9.22) * mm});
            skArc(sketch, "E57.3.0", {"start": v(-17.36, -30.4) * mm, "mid": v(-18.17, -18.17) * mm, "end": v(-30.4, -17.36) * mm});
            skArc(sketch, "E57.4.0", {"start": v(9.22, -33.76) * mm, "mid": v(0, -25.7) * mm, "end": v(-9.22, -33.76) * mm});
            skArc(sketch, "E57.5.0", {"start": v(30.4, -17.36) * mm, "mid": v(18.17, -18.17) * mm, "end": v(17.36, -30.4) * mm});
            skArc(sketch, "E57.6.0", {"start": v(33.76, 9.22) * mm, "mid": v(25.7, 0) * mm, "end": v(33.76, -9.22) * mm});
            skArc(sketch, "E57.7.0", {"start": v(17.36, 30.4) * mm, "mid": v(18.17, 18.17) * mm, "end": v(30.4, 17.36) * mm});
            skSolve(sketch);
        }
        {
            var Q0;
            {var subQ6=sQuery(id+"F8.wireOp",EDGE,"E56");Q0=makeQuery(id+"F8.imprint","IMPRINT",FACE,{"disambiguationData":[TD([[makeQuery(id+"F8.imprint","IMPRINT",EDGE,{"derivedFrom":subQ6}),-1.0]])]});}
            extrude(context, id + "F9", {"entities" : qUnion([Q0]), "depth" : 3 * mm});
        }
        {
            var Q0;
            Q0=qCreatedBy(makeId("Top.planeOp"),FACE);
            var sketch = newSketch(context, id + "F10", { "sketchPlane" : qUnion([Q0])});
            skCircle(sketch, "E58", {"center": v(-104.85, 0) * mm, "radius": 5.9 * mm});
            skCircle(sketch, "E59", {"center": v(-104.85, 0) * mm, "radius": 11 * mm});
            skSolve(sketch);
        }
        {
            var Q0;
            Q0=makeQuery(id+"F10.imprint","IMPRINT",FACE,{"disambiguationData":[TD([[makeQuery(id+"F10.imprint","IMPRINT",EDGE,{"derivedFrom":sQuery(id+"F10.wireOp",EDGE,"E58")}),-1.0]])]});
            extrude(context, id + "F11", {"entities" : qUnion([Q0]), "depth" : 3 * mm});
        }
    });
